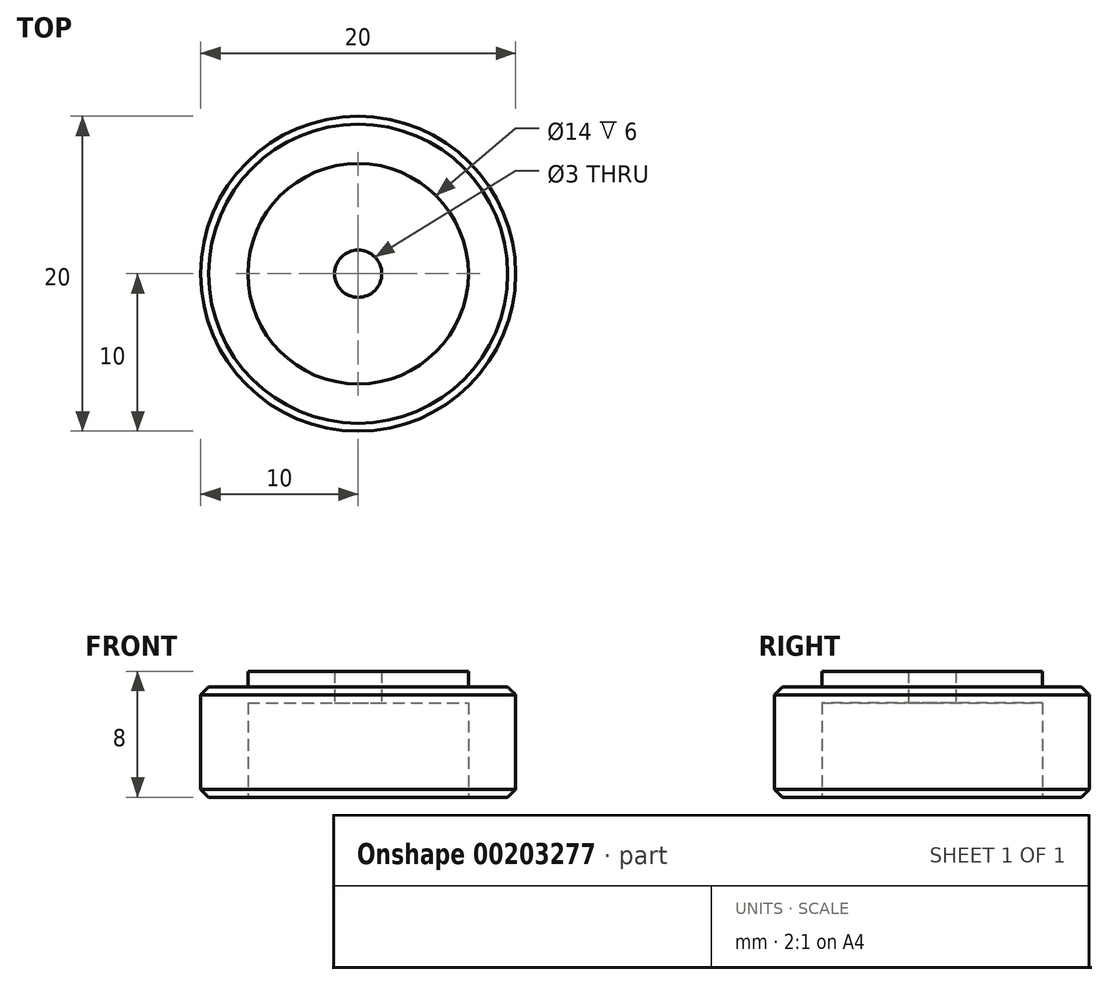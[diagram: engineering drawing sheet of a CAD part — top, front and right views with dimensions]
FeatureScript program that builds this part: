
annotation { "Feature Type Name" : "Feature", "Feature Type Description" : "" }
export const myFeature = defineFeature(function(context is Context, id is Id, definition is map)
    precondition{}
    {
        {
            var Q0;
            Q0=qCreatedBy(makeId("Top.planeOp"),FACE);
            var sketch = newSketch(context, id + "F0", { "sketchPlane" : qUnion([Q0])});
            skCircle(sketch, "E0", {"center": v(0, 0) * mm, "radius": 10 * mm});
            skCircle(sketch, "E1", {"center": v(0, 0) * mm, "radius": 7 * mm});
            skSolve(sketch);
        }
        {
            var Q0;
            Q0=makeQuery(id+"F0.imprint","IMPRINT",FACE,{"disambiguationData":[TD([[makeQuery(id+"F0.imprint","IMPRINT",EDGE,{"derivedFrom":sQuery(id+"F0.wireOp",EDGE,"E1")}),1.0]])]});
            extrude(context, id + "F1", {"entities" : qUnion([Q0]), "depth" : 1 * mm});
        }
        {
            var Q0;
            Q0=makeQuery(id+"F0.imprint","IMPRINT",FACE,{"disambiguationData":[TD([[makeQuery(id+"F0.imprint","IMPRINT",EDGE,{"derivedFrom":sQuery(id+"F0.wireOp",EDGE,"E1")}),1.0]])]});
            var Q1;
            Q1=makeQuery(id+"F0.imprint","IMPRINT",FACE,{"disambiguationData":[TD([[makeQuery(id+"F0.imprint","IMPRINT",EDGE,{"derivedFrom":sQuery(id+"F0.wireOp",EDGE,"E0")}),1.0]])]});
            extrude(context, id + "F2", {"entities" : qUnion([Q0, Q1]), "operationType" : NewBodyOperationType.ADD, "oppositeDirection" : true, "depth" : 7 * mm});
        }
        {
            var Q0;
            Q0=makeQuery(id+"F2.opExtrude","CAP_EDGE",EDGE,{"disambiguationData":[OSD([sQuery(id+"F0.wireOp",EDGE,"E0")])],"isStart":true});
            var Q1;
            Q1=makeQuery(id+"F2.opExtrude","CAP_EDGE",EDGE,{"disambiguationData":[OSD([sQuery(id+"F0.wireOp",EDGE,"E0")])],"isStart":false});
            chamfer(context, id + "F3", {"entities" : qUnion([Q0, Q1]), "width" : .5 * mm, "tangentPropagation" : true});
        }
        {
            var Q0;
            Q0=makeQuery(id+"F2.opExtrude","CAP_FACE",FACE,{"disambiguationData":[OSD([sQuery(id+"F0.wireOp",EDGE,"E0")])],"isStart":false});
            var sketch = newSketch(context, id + "F4", { "sketchPlane" : qUnion([Q0])});
            skCircle(sketch, "E2", {"center": v(0, 0) * mm, "radius": 7 * mm});
            skCircle(sketch, "E3", {"center": v(0, 0) * mm, "radius": 1.5 * mm});
            skSolve(sketch);
        }
        {
            var Q0;
            Q0=makeQuery(id+"F4.imprint","IMPRINT",FACE,{"disambiguationData":[TD([[makeQuery(id+"F4.imprint","IMPRINT",EDGE,{"derivedFrom":sQuery(id+"F4.wireOp",EDGE,"E3")}),1.0]])]});
            var Q1;
            Q1=makeQuery(id+"F4.imprint","IMPRINT",FACE,{"disambiguationData":[TD([[makeQuery(id+"F4.imprint","IMPRINT",EDGE,{"derivedFrom":sQuery(id+"F4.wireOp",EDGE,"E2")}),1.0]])]});
            extrude(context, id + "F5", {"entities" : qUnion([Q0, Q1]), "operationType" : NewBodyOperationType.REMOVE, "oppositeDirection" : true, "depth" : 6 * mm});
        }
        {
            var Q0;
            Q0=makeQuery(id+"F4.imprint","IMPRINT",FACE,{"disambiguationData":[TD([[makeQuery(id+"F4.imprint","IMPRINT",EDGE,{"derivedFrom":sQuery(id+"F4.wireOp",EDGE,"E3")}),1.0]])]});
            extrude(context, id + "F6", {"entities" : qUnion([Q0]), "operationType" : NewBodyOperationType.REMOVE, "oppositeDirection" : true, "depth" : 25 * mm});
        }
    });
